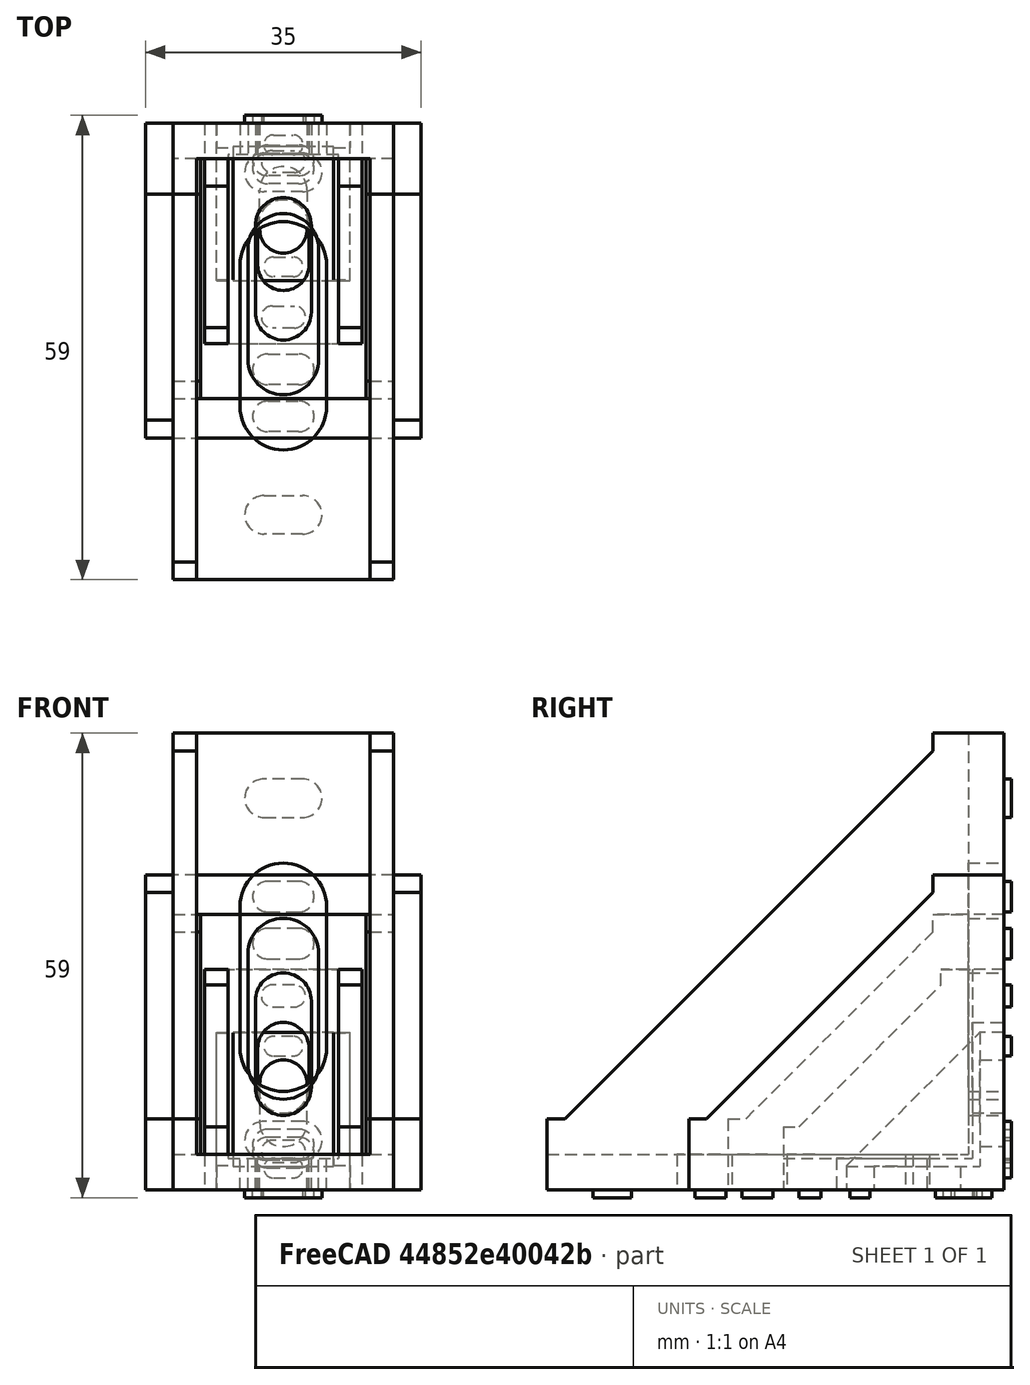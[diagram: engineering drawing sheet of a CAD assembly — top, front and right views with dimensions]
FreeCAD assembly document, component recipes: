
FREECAD ASSEMBLY — COMPONENT RECIPES ("Corner_bracket")

This assembly document has 5 components, labeled P0..P4 below (a component is one placed body or linked part). 5 of them carry a construction recipe — the FreeCAD feature program that regenerates the part from scratch, quoted from this document or its linked companion documents; the rest are supplied as boundary geometry only. No exploded tour is included for this assembly.
COMPONENT P0 — recipe-attached ("Corner bracket001", modeled in this document).
Construction recipe (the document's own serialized feature program — sketch geometry with constraints, then the solid features built on it; lengths are millimeters unless a unit is written):

FEATURE [PartDesign::Plane] DatumPlane001
  AttachmentOffset = pos=(0,0,0) rot=(1,0,0;0.785398rad)
  Length = 65.3219
  MapMode = 5
  Placement = pos=(0,0,0) rot=(1,0,0;2.35619rad)
  ResizeMode = 0
  Support = -> [XZ_Plane003]
  Width = 132.702
FEATURE [Sketcher::SketchObject] Sketch004
  FullyConstrained = true
  MapMode = 5
  Placement = pos=(0,0,0) rot=(1,0,0;1.5708rad)
  Support = -> [XZ_Plane003]
  expr: Constraints[7] = <<Spreadsheet001>>.E_dim
  expr: Constraints[8] = <<Spreadsheet001>>.F_dim
  expr: Constraints[9] = <<Spreadsheet001>>.H_dim
  sketch-geometry (4):
    g0: ArcOfCircle CenterX=0 CenterY=8.5 CenterZ=0 NormalX=0 NormalY=0 NormalZ=1 AngleXU=0 Radius=3 StartAngle=3.14159 EndAngle=6.28319
    g1: ArcOfCircle CenterX=0 CenterY=13.5 CenterZ=0 NormalX=0 NormalY=0 NormalZ=1 AngleXU=0 Radius=3 StartAngle=0 EndAngle=3.14159
    g2: LineSegment StartX=3 StartY=8.5 StartZ=0 EndX=3 EndY=13.5 EndZ=0
    g3: LineSegment StartX=-3 StartY=13.5 StartZ=0 EndX=-3 EndY=8.5 EndZ=0
  constraints (10):
    c: Tangent(g0,g2) = -1.5708
    c: Tangent(g2,g1) = -1.5708
    c: Tangent(g1,g3) = -1.5708
    c: Tangent(g3,g0) = -1.5708
    c: Equal(g0,g1)
    c: PointOnObject(g0,g-2)
    c: PointOnObject(g1,g-2)
    c: DistanceY(g0) = 8.5
    c: DistanceY(g2,g2) = 5
    c: Diameter(g1) = 6
FEATURE [Sketcher::SketchObject] Sketch005
  FullyConstrained = true
  MapMode = 5
  Placement = pos=(0,0,0) rot=(0.57735,0.57735,0.57735;2.0944rad)
  Support = -> [YZ_Plane003]
  expr: Constraints[10] = <<Spreadsheet001>>.A_dim
  expr: Constraints[15] = <<Spreadsheet001>>.D_aux2
  expr: Constraints[8] = <<Spreadsheet001>>.A_dim
  expr: Constraints[9] = <<Spreadsheet001>>.D_dim + <<Spreadsheet001>>.D_aux1
  sketch-geometry (7):
    g0: LineSegment StartX=0 StartY=0 StartZ=0 EndX=0 EndY=20 EndZ=0
    g1: LineSegment StartX=0 StartY=20 StartZ=0 EndX=-3.1 EndY=20 EndZ=0
    g2: LineSegment StartX=-20 StartY=3.1 StartZ=0 EndX=-20 EndY=0 EndZ=0
    g3: LineSegment StartX=-20 StartY=0 StartZ=0 EndX=0 EndY=0 EndZ=0
    g4: LineSegment StartX=-20 StartY=3.1 StartZ=0 EndX=-19.9 EndY=3.1 EndZ=0
    g5: LineSegment StartX=-19.9 StartY=3.1 StartZ=0 EndX=-3.1 EndY=19.9 EndZ=0
    g6: LineSegment StartX=-3.1 StartY=19.9 StartZ=0 EndX=-3.1 EndY=20 EndZ=0
  constraints (20):
    c: Coincident(g-1,g0)
    c: PointOnObject(g0,g-2)
    c: Coincident(g0,g1)
    c: Horizontal(g1)
    c: PointOnObject(g2,g-1)
    c: Vertical(g2)
    c: Coincident(g2,g3)
    c: Coincident(g3,g0)
    c: DistanceY(g0,g0) = 20
    c: DistanceX(g1,g1) = 3.1
    c: DistanceX(g3,g3) = 20
    c: Coincident(g2,g4)
    c: Horizontal(g4)
    c: Coincident(g4,g5)
    c: Equal(g2,g1)
    c: DistanceX(g4,g4) = 0.1
    c: Angle(g5) = 0.785398
    c: Coincident(g6,g5)
    c: Coincident(g6,g1)
    c: Vertical(g6)
FEATURE [PartDesign::Pad] Pad002
  Direction = (1,-2e-16,3e-16)
  Length = 17
  Length2 = 100
  Midplane = true
  Placement = pos=(0,0,0) rot=(0.57735,0.57735,0.57735;2.0944rad)
  Profile = -> Sketch005
  ReferenceAxis = -> Sketch005 [N_Axis]
  Type = 0
  expr: Length = <<Spreadsheet001>>.B_dim
FEATURE [Sketcher::SketchObject] Sketch006
  ExternalGeometry = -> [Pad002]
  FullyConstrained = true
  MapMode = 5
  Placement = pos=(-7.8e-15,1.11e-14,20) rot=(0,0,-1;1.5708rad)
  Support = -> [Pad002]
  expr: Constraints[10] = <<Spreadsheet001>>.D_dim
  expr: Constraints[12] = <<Spreadsheet001>>.C_dim
  sketch-geometry (5):
    g0: LineSegment StartX=20 StartY=-6.4 StartZ=0 EndX=20 EndY=6.4 EndZ=0
    g1: LineSegment StartX=20 StartY=6.4 StartZ=0 EndX=3 EndY=6.4 EndZ=0
    g2: LineSegment StartX=3 StartY=6.4 StartZ=0 EndX=3 EndY=-6.4 EndZ=0
    g3: LineSegment StartX=3 StartY=-6.4 StartZ=0 EndX=20 EndY=-6.4 EndZ=0
    g4: GeomPoint X=11.5 Y=0 Z=0
  constraints (13):
    c: Coincident(g0,g1)
    c: Coincident(g1,g2)
    c: Coincident(g2,g3)
    c: Coincident(g3,g0)
    c: Horizontal(g1)
    c: Horizontal(g3)
    c: Vertical(g0)
    c: Vertical(g2)
    c: Symmetric(g1,g0,g4)
    c: PointOnObject(g4,g-1)
    c: DistanceX(g1) = 3
    c: Vertical(g0,g-3)
    c: DistanceY(g0,g0) = 12.8
FEATURE [PartDesign::Pocket] Pocket002
  BaseFeature = -> Pad002
  Direction = (4e-16,-6e-16,-1)
  Length = 17
  Length2 = 5
  Placement = pos=(0,0,0) rot=(0.57735,0.57735,0.57735;2.0944rad)
  Profile = -> Sketch006
  ReferenceAxis = -> Sketch006 [N_Axis]
  Type = 0
  expr: Length = <<Spreadsheet001>>.A_dim - <<Spreadsheet001>>.D_dim
FEATURE [PartDesign::Pocket] Pocket003
  BaseFeature = -> Pocket002
  Direction = (0,1,2e-16)
  Length = 5
  Length2 = 5
  Placement = pos=(0,0,0) rot=(0.57735,0.57735,0.57735;2.0944rad)
  Profile = -> Sketch004
  ReferenceAxis = -> Sketch004 [N_Axis]
  Reversed = true
  Type = 2
FEATURE [Sketcher::SketchObject] Sketch007
  FullyConstrained = true
  MapMode = 5
  Placement = pos=(0,0,0) rot=(1,0,0;1.5708rad)
  Support = -> [XZ_Plane003]
  expr: Constraints[14] = <<Spreadsheet001>>.G_dim / 2
  expr: Constraints[15] = <<Spreadsheet001>>.G_dim / 4
  expr: Constraints[16] = (<<Spreadsheet001>>.E_dim - <<Spreadsheet001>>.H_dim / 2) / 2
  expr: Constraints[17] = (<<Spreadsheet001>>.A_dim + <<Spreadsheet001>>.E_dim + <<Spreadsheet001>>.F_dim + <<Spreadsheet001>>.H_dim / 2) / 2
  sketch-geometry (8):
    g0: ArcOfCircle CenterX=-1.25 CenterY=2.75 CenterZ=0 NormalX=0 NormalY=0 NormalZ=1 AngleXU=0 Radius=1.25 StartAngle=1.5708 EndAngle=4.71239
    g1: ArcOfCircle CenterX=1.25 CenterY=2.75 CenterZ=0 NormalX=0 NormalY=0 NormalZ=1 AngleXU=0 Radius=1.25 StartAngle=4.71239 EndAngle=7.85398
    g2: LineSegment StartX=-1.25 StartY=1.5 StartZ=0 EndX=1.25 EndY=1.5 EndZ=0
    g3: LineSegment StartX=1.25 StartY=4 StartZ=0 EndX=-1.25 EndY=4 EndZ=0
    g4: ArcOfCircle CenterX=-1.25 CenterY=18.25 CenterZ=0 NormalX=0 NormalY=0 NormalZ=1 AngleXU=0 Radius=1.25 StartAngle=1.5708 EndAngle=4.71239
    g5: ArcOfCircle CenterX=1.25 CenterY=18.25 CenterZ=0 NormalX=0 NormalY=0 NormalZ=1 AngleXU=0 Radius=1.25 StartAngle=4.71239 EndAngle=7.85398
    g6: LineSegment StartX=-1.25 StartY=17 StartZ=0 EndX=1.25 EndY=17 EndZ=0
    g7: LineSegment StartX=1.25 StartY=19.5 StartZ=0 EndX=-1.25 EndY=19.5 EndZ=0
  constraints (18):
    c: Tangent(g0,g2) = -1.5708
    c: Tangent(g2,g1) = -1.5708
    c: Tangent(g1,g3) = -1.5708
    c: Tangent(g3,g0) = -1.5708
    c: Equal(g0,g1)
    c: Tangent(g4,g6) = -1.5708
    c: Tangent(g6,g5) = -1.5708
    c: Tangent(g5,g7) = -1.5708
    c: Tangent(g7,g4) = -1.5708
    c: Equal(g4,g5)
    c: Symmetric(g1,g0,g-2)
    c: Symmetric(g4,g5,g-2)
    c: Equal(g7,g2)
    c: Equal(g1,g5)
    c: DistanceX(g7,g7) = 2.5
    c: Radius(g5) = 1.25
    c: DistanceY(g1) = 2.75
    c: DistanceY(g4) = 18.25
FEATURE [PartDesign::Pad] Pad003
  BaseFeature = -> Pocket003
  Direction = (0,-1,-2e-16)
  Length = 1
  Length2 = 10
  Placement = pos=(0,0,0) rot=(0.57735,0.57735,0.57735;2.0944rad)
  Profile = -> Sketch007
  ReferenceAxis = -> Sketch007 [N_Axis]
  Reversed = true
  Type = 0
FEATURE [PartDesign::Mirrored] Mirrored001
  BaseFeature = -> Pad003
  MirrorPlane = -> DatumPlane001
  Originals = -> [Pocket003,Pad003]
  Placement = pos=(0,0,0) rot=(0.57735,0.57735,0.57735;2.0944rad)
FEATURE [PartDesign::Body] Body001  label="Corner bracket 20x20"
  Group = -> [Sketch005,Pad002,Sketch006,Pocket002,Sketch004,Pocket003,Sketch007,Pad003,DatumPlane001,Mirrored001]
  Origin = -> Origin003
  Tip = -> Mirrored001
  expr: Label = <<Corner bracket %s>> % Spreadsheet001.A_dim + <<x%s>> % Spreadsheet001.A_dim
COMPONENT P1 — recipe-attached ("Corner bracket002", modeled in this document).
Construction recipe (the document's own serialized feature program — sketch geometry with constraints, then the solid features built on it; lengths are millimeters unless a unit is written):

FEATURE [PartDesign::Plane] DatumPlane002
  AttachmentOffset = pos=(0,0,0) rot=(1,0,0;0.785398rad)
  Length = 65.3219
  MapMode = 5
  Placement = pos=(0,0,0) rot=(1,0,0;2.35619rad)
  ResizeMode = 0
  Support = -> [XZ_Plane005]
  Width = 132.702
FEATURE [Sketcher::SketchObject] Sketch008
  FullyConstrained = true
  MapMode = 5
  Placement = pos=(0,0,0) rot=(1,0,0;1.5708rad)
  Support = -> [XZ_Plane005]
  expr: Constraints[7] = <<Spreadsheet002>>.E_dim
  expr: Constraints[8] = <<Spreadsheet002>>.F_dim
  expr: Constraints[9] = <<Spreadsheet002>>.H_dim
  sketch-geometry (4):
    g0: ArcOfCircle CenterX=0 CenterY=13 CenterZ=0 NormalX=0 NormalY=0 NormalZ=1 AngleXU=0 Radius=3.25 StartAngle=3.14159 EndAngle=6.28319
    g1: ArcOfCircle CenterX=0 CenterY=18 CenterZ=0 NormalX=0 NormalY=0 NormalZ=1 AngleXU=0 Radius=3.25 StartAngle=7.603e-13 EndAngle=3.14159
    g2: LineSegment StartX=3.25 StartY=13 StartZ=0 EndX=3.25 EndY=18 EndZ=0
    g3: LineSegment StartX=-3.25 StartY=18 StartZ=0 EndX=-3.25 EndY=13 EndZ=0
  constraints (10):
    c: Tangent(g0,g2) = -1.5708
    c: Tangent(g2,g1) = -1.5708
    c: Tangent(g1,g3) = -1.5708
    c: Tangent(g3,g0) = -1.5708
    c: Equal(g0,g1)
    c: PointOnObject(g0,g-2)
    c: PointOnObject(g1,g-2)
    c: DistanceY(g0) = 13
    c: DistanceY(g2,g2) = 5
    c: Diameter(g1) = 6.5
FEATURE [Sketcher::SketchObject] Sketch009
  FullyConstrained = true
  MapMode = 5
  Placement = pos=(0,0,0) rot=(0.57735,0.57735,0.57735;2.0944rad)
  Support = -> [YZ_Plane005]
  expr: Constraints[10] = <<Spreadsheet002>>.A_dim
  expr: Constraints[15] = <<Spreadsheet002>>.D_aux2
  expr: Constraints[8] = <<Spreadsheet002>>.A_dim
  expr: Constraints[9] = <<Spreadsheet002>>.D_dim + <<Spreadsheet002>>.D_aux1
  sketch-geometry (7):
    g0: LineSegment StartX=0 StartY=0 StartZ=0 EndX=0 EndY=28 EndZ=0
    g1: LineSegment StartX=0 StartY=28 StartZ=0 EndX=-8 EndY=28 EndZ=0
    g2: LineSegment StartX=-28 StartY=8 StartZ=0 EndX=-28 EndY=0 EndZ=0
    g3: LineSegment StartX=-28 StartY=0 StartZ=0 EndX=0 EndY=0 EndZ=0
    g4: LineSegment StartX=-28 StartY=8 StartZ=0 EndX=-26 EndY=8 EndZ=0
    g5: LineSegment StartX=-26 StartY=8 StartZ=0 EndX=-8 EndY=26 EndZ=0
    g6: LineSegment StartX=-8 StartY=26 StartZ=0 EndX=-8 EndY=28 EndZ=0
  constraints (20):
    c: Coincident(g-1,g0)
    c: PointOnObject(g0,g-2)
    c: Coincident(g0,g1)
    c: Horizontal(g1)
    c: PointOnObject(g2,g-1)
    c: Vertical(g2)
    c: Coincident(g2,g3)
    c: Coincident(g3,g0)
    c: DistanceY(g0,g0) = 28
    c: DistanceX(g1,g1) = 8
    c: DistanceX(g3,g3) = 28
    c: Coincident(g2,g4)
    c: Horizontal(g4)
    c: Coincident(g4,g5)
    c: Equal(g2,g1)
    c: DistanceX(g4,g4) = 2
    c: Angle(g5) = 0.785398
    c: Coincident(g6,g5)
    c: Coincident(g6,g1)
    c: Vertical(g6)
FEATURE [PartDesign::Pad] Pad004
  Direction = (1,-2e-16,3e-16)
  Length = 20
  Length2 = 100
  Midplane = true
  Placement = pos=(0,0,0) rot=(0.57735,0.57735,0.57735;2.0944rad)
  Profile = -> Sketch009
  ReferenceAxis = -> Sketch009 [N_Axis]
  Type = 0
  expr: Length = <<Spreadsheet002>>.B_dim
FEATURE [Sketcher::SketchObject] Sketch010
  ExternalGeometry = -> [Pad004]
  FullyConstrained = true
  MapMode = 5
  Placement = pos=(-1.09e-14,1.55e-14,28) rot=(0,0,-1;1.5708rad)
  Support = -> [Pad004]
  expr: Constraints[10] = <<Spreadsheet002>>.D_dim
  expr: Constraints[12] = <<Spreadsheet002>>.C_dim
  sketch-geometry (5):
    g0: LineSegment StartX=28 StartY=-7 StartZ=0 EndX=28 EndY=7 EndZ=0
    g1: LineSegment StartX=28 StartY=7 StartZ=0 EndX=4 EndY=7 EndZ=0
    g2: LineSegment StartX=4 StartY=7 StartZ=0 EndX=4 EndY=-7 EndZ=0
    g3: LineSegment StartX=4 StartY=-7 StartZ=0 EndX=28 EndY=-7 EndZ=0
    g4: GeomPoint X=16 Y=0 Z=0
  constraints (13):
    c: Coincident(g0,g1)
    c: Coincident(g1,g2)
    c: Coincident(g2,g3)
    c: Coincident(g3,g0)
    c: Horizontal(g1)
    c: Horizontal(g3)
    c: Vertical(g0)
    c: Vertical(g2)
    c: Symmetric(g1,g0,g4)
    c: PointOnObject(g4,g-1)
    c: DistanceX(g1) = 4
    c: Vertical(g0,g-3)
    c: DistanceY(g0,g0) = 14
FEATURE [PartDesign::Pocket] Pocket004
  BaseFeature = -> Pad004
  Direction = (4e-16,-6e-16,-1)
  Length = 24
  Length2 = 5
  Placement = pos=(0,0,0) rot=(0.57735,0.57735,0.57735;2.0944rad)
  Profile = -> Sketch010
  ReferenceAxis = -> Sketch010 [N_Axis]
  Type = 0
  expr: Length = <<Spreadsheet002>>.A_dim - <<Spreadsheet002>>.D_dim
FEATURE [PartDesign::Pocket] Pocket005
  BaseFeature = -> Pocket004
  Direction = (0,1,2e-16)
  Length = 5
  Length2 = 5
  Placement = pos=(0,0,0) rot=(0.57735,0.57735,0.57735;2.0944rad)
  Profile = -> Sketch008
  ReferenceAxis = -> Sketch008 [N_Axis]
  Reversed = true
  Type = 2
FEATURE [Sketcher::SketchObject] Sketch011
  FullyConstrained = true
  MapMode = 5
  Placement = pos=(0,0,0) rot=(1,0,0;1.5708rad)
  Support = -> [XZ_Plane005]
  expr: Constraints[14] = <<Spreadsheet002>>.G_dim / 2
  expr: Constraints[15] = <<Spreadsheet002>>.G_dim / 4
  expr: Constraints[16] = (<<Spreadsheet002>>.E_dim - <<Spreadsheet002>>.H_dim / 2) / 2
  expr: Constraints[17] = (<<Spreadsheet002>>.A_dim + <<Spreadsheet002>>.E_dim + <<Spreadsheet002>>.F_dim + <<Spreadsheet002>>.H_dim / 2) / 2
  sketch-geometry (8):
    g0: ArcOfCircle CenterX=-1.4 CenterY=4.875 CenterZ=0 NormalX=0 NormalY=0 NormalZ=1 AngleXU=0 Radius=1.4 StartAngle=1.5708 EndAngle=4.71239
    g1: ArcOfCircle CenterX=1.4 CenterY=4.875 CenterZ=0 NormalX=0 NormalY=0 NormalZ=1 AngleXU=0 Radius=1.4 StartAngle=4.71239 EndAngle=7.85398
    g2: LineSegment StartX=-1.4 StartY=3.475 StartZ=0 EndX=1.4 EndY=3.475 EndZ=0
    g3: LineSegment StartX=1.4 StartY=6.275 StartZ=0 EndX=-1.4 EndY=6.275 EndZ=0
    g4: ArcOfCircle CenterX=-1.4 CenterY=24.625 CenterZ=0 NormalX=0 NormalY=0 NormalZ=1 AngleXU=0 Radius=1.4 StartAngle=1.5708 EndAngle=4.71239
    g5: ArcOfCircle CenterX=1.4 CenterY=24.625 CenterZ=0 NormalX=0 NormalY=0 NormalZ=1 AngleXU=0 Radius=1.4 StartAngle=4.71239 EndAngle=7.85398
    g6: LineSegment StartX=-1.4 StartY=23.225 StartZ=0 EndX=1.4 EndY=23.225 EndZ=0
    g7: LineSegment StartX=1.4 StartY=26.025 StartZ=0 EndX=-1.4 EndY=26.025 EndZ=0
  constraints (18):
    c: Tangent(g0,g2) = -1.5708
    c: Tangent(g2,g1) = -1.5708
    c: Tangent(g1,g3) = -1.5708
    c: Tangent(g3,g0) = -1.5708
    c: Equal(g0,g1)
    c: Tangent(g4,g6) = -1.5708
    c: Tangent(g6,g5) = -1.5708
    c: Tangent(g5,g7) = -1.5708
    c: Tangent(g7,g4) = -1.5708
    c: Equal(g4,g5)
    c: Symmetric(g1,g0,g-2)
    c: Symmetric(g4,g5,g-2)
    c: Equal(g7,g2)
    c: Equal(g1,g5)
    c: DistanceX(g7,g7) = 2.8
    c: Radius(g5) = 1.4
    c: DistanceY(g1) = 4.875
    c: DistanceY(g4) = 24.625
FEATURE [PartDesign::Pad] Pad005
  BaseFeature = -> Pocket005
  Direction = (0,-1,-2e-16)
  Length = 1
  Length2 = 10
  Placement = pos=(0,0,0) rot=(0.57735,0.57735,0.57735;2.0944rad)
  Profile = -> Sketch011
  ReferenceAxis = -> Sketch011 [N_Axis]
  Reversed = true
  Type = 0
FEATURE [PartDesign::Mirrored] Mirrored002
  BaseFeature = -> Pad005
  MirrorPlane = -> DatumPlane002
  Originals = -> [Pocket005,Pad005]
  Placement = pos=(0,0,0) rot=(0.57735,0.57735,0.57735;2.0944rad)
FEATURE [PartDesign::Body] Body002  label="Corner bracket 28x28"
  Group = -> [Sketch009,Pad004,Sketch010,Pocket004,Sketch008,Pocket005,Sketch011,Pad005,DatumPlane002,Mirrored002]
  Origin = -> Origin005
  Tip = -> Mirrored002
  expr: Label = <<Corner bracket %s>> % Spreadsheet002.A_dim + <<x%s>> % Spreadsheet002.A_dim
COMPONENT P2 — recipe-attached ("Corner bracket003", modeled in this document).
Construction recipe (the document's own serialized feature program — sketch geometry with constraints, then the solid features built on it; lengths are millimeters unless a unit is written):

FEATURE [PartDesign::Plane] DatumPlane003
  AttachmentOffset = pos=(0,0,0) rot=(1,0,0;0.785398rad)
  Length = 63.0271
  MapMode = 5
  Placement = pos=(0,0,0) rot=(1,0,0;2.35619rad)
  ResizeMode = 0
  Support = -> [XZ_Plane007]
  Width = 97.8799
FEATURE [Sketcher::SketchObject] Sketch012
  FullyConstrained = true
  MapMode = 5
  Placement = pos=(0,0,0) rot=(1,0,0;1.5708rad)
  Support = -> [XZ_Plane007]
  expr: Constraints[7] = <<Spreadsheet003>>.E_dim
  expr: Constraints[8] = <<Spreadsheet003>>.F_dim
  expr: Constraints[9] = <<Spreadsheet003>>.H_dim
  sketch-geometry (4):
    g0: ArcOfCircle CenterX=0 CenterY=18 CenterZ=0 NormalX=0 NormalY=0 NormalZ=1 AngleXU=0 Radius=5.5 StartAngle=3.14159 EndAngle=6.28319
    g1: ArcOfCircle CenterX=0 CenterY=36 CenterZ=0 NormalX=0 NormalY=0 NormalZ=1 AngleXU=0 Radius=5.5 StartAngle=-5.3e-15 EndAngle=3.14159
    g2: LineSegment StartX=5.5 StartY=18 StartZ=0 EndX=5.5 EndY=36 EndZ=0
    g3: LineSegment StartX=-5.5 StartY=36 StartZ=0 EndX=-5.5 EndY=18 EndZ=0
  constraints (10):
    c: Tangent(g0,g2) = -1.5708
    c: Tangent(g2,g1) = -1.5708
    c: Tangent(g1,g3) = -1.5708
    c: Tangent(g3,g0) = -1.5708
    c: Equal(g0,g1)
    c: PointOnObject(g0,g-2)
    c: PointOnObject(g1,g-2)
    c: DistanceY(g0) = 18
    c: DistanceY(g2,g2) = 18
    c: Diameter(g1) = 11
FEATURE [Sketcher::SketchObject] Sketch013
  FullyConstrained = true
  MapMode = 5
  Placement = pos=(0,0,0) rot=(0.57735,0.57735,0.57735;2.0944rad)
  Support = -> [YZ_Plane007]
  expr: Constraints[10] = <<Spreadsheet003>>.A_dim
  expr: Constraints[15] = <<Spreadsheet003>>.D_aux2
  expr: Constraints[8] = <<Spreadsheet003>>.A_dim
  expr: Constraints[9] = <<Spreadsheet003>>.D_dim + <<Spreadsheet003>>.D_aux1
  sketch-geometry (7):
    g0: LineSegment StartX=0 StartY=0 StartZ=0 EndX=0 EndY=58 EndZ=0
    g1: LineSegment StartX=0 StartY=58 StartZ=0 EndX=-9 EndY=58 EndZ=0
    g2: LineSegment StartX=-58 StartY=9 StartZ=0 EndX=-58 EndY=0 EndZ=0
    g3: LineSegment StartX=-58 StartY=0 StartZ=0 EndX=0 EndY=0 EndZ=0
    g4: LineSegment StartX=-58 StartY=9 StartZ=0 EndX=-55.75 EndY=9 EndZ=0
    g5: LineSegment StartX=-55.75 StartY=9 StartZ=0 EndX=-9 EndY=55.75 EndZ=0
    g6: LineSegment StartX=-9 StartY=55.75 StartZ=0 EndX=-9 EndY=58 EndZ=0
  constraints (20):
    c: Coincident(g-1,g0)
    c: PointOnObject(g0,g-2)
    c: Coincident(g0,g1)
    c: Horizontal(g1)
    c: PointOnObject(g2,g-1)
    c: Vertical(g2)
    c: Coincident(g2,g3)
    c: Coincident(g3,g0)
    c: DistanceY(g0,g0) = 58
    c: DistanceX(g1,g1) = 9
    c: DistanceX(g3,g3) = 58
    c: Coincident(g2,g4)
    c: Horizontal(g4)
    c: Coincident(g4,g5)
    c: Equal(g2,g1)
    c: DistanceX(g4,g4) = 2.25
    c: Angle(g5) = 0.785398
    c: Coincident(g6,g5)
    c: Coincident(g6,g1)
    c: Vertical(g6)
FEATURE [PartDesign::Pad] Pad006
  Direction = (1,-2e-16,3e-16)
  Length = 28
  Length2 = 100
  Midplane = true
  Placement = pos=(0,0,0) rot=(0.57735,0.57735,0.57735;2.0944rad)
  Profile = -> Sketch013
  ReferenceAxis = -> Sketch013 [N_Axis]
  Type = 0
  expr: Length = <<Spreadsheet003>>.B_dim
FEATURE [Sketcher::SketchObject] Sketch014
  ExternalGeometry = -> [Pad006]
  FullyConstrained = true
  MapMode = 5
  Placement = pos=(-2.25e-14,3.22e-14,58) rot=(0,0,-1;1.5708rad)
  Support = -> [Pad006]
  expr: Constraints[10] = <<Spreadsheet003>>.D_dim
  expr: Constraints[12] = <<Spreadsheet003>>.C_dim
  sketch-geometry (5):
    g0: LineSegment StartX=58 StartY=-11 StartZ=0 EndX=58 EndY=11 EndZ=0
    g1: LineSegment StartX=58 StartY=11 StartZ=0 EndX=4.5 EndY=11 EndZ=0
    g2: LineSegment StartX=4.5 StartY=11 StartZ=0 EndX=4.5 EndY=-11 EndZ=0
    g3: LineSegment StartX=4.5 StartY=-11 StartZ=0 EndX=58 EndY=-11 EndZ=0
    g4: GeomPoint X=31.25 Y=0 Z=0
  constraints (13):
    c: Coincident(g0,g1)
    c: Coincident(g1,g2)
    c: Coincident(g2,g3)
    c: Coincident(g3,g0)
    c: Horizontal(g1)
    c: Horizontal(g3)
    c: Vertical(g0)
    c: Vertical(g2)
    c: Symmetric(g1,g0,g4)
    c: PointOnObject(g4,g-1)
    c: DistanceX(g1) = 4.5
    c: Vertical(g0,g-3)
    c: DistanceY(g0,g0) = 22
FEATURE [PartDesign::Pocket] Pocket006
  BaseFeature = -> Pad006
  Direction = (4e-16,-6e-16,-1)
  Length = 53.5
  Length2 = 5
  Placement = pos=(0,0,0) rot=(0.57735,0.57735,0.57735;2.0944rad)
  Profile = -> Sketch014
  ReferenceAxis = -> Sketch014 [N_Axis]
  Type = 0
  expr: Length = <<Spreadsheet003>>.A_dim - <<Spreadsheet003>>.D_dim
FEATURE [PartDesign::Pocket] Pocket007
  BaseFeature = -> Pocket006
  Direction = (0,1,2e-16)
  Length = 5
  Length2 = 5
  Placement = pos=(0,0,0) rot=(0.57735,0.57735,0.57735;2.0944rad)
  Profile = -> Sketch012
  ReferenceAxis = -> Sketch012 [N_Axis]
  Reversed = true
  Type = 2
FEATURE [Sketcher::SketchObject] Sketch015
  FullyConstrained = true
  MapMode = 5
  Placement = pos=(0,0,0) rot=(1,0,0;1.5708rad)
  Support = -> [XZ_Plane007]
  expr: Constraints[14] = <<Spreadsheet003>>.G_dim / 2
  expr: Constraints[15] = <<Spreadsheet003>>.G_dim / 4
  expr: Constraints[16] = (<<Spreadsheet003>>.E_dim - <<Spreadsheet003>>.H_dim / 2) / 2
  expr: Constraints[17] = (<<Spreadsheet003>>.A_dim + <<Spreadsheet003>>.E_dim + <<Spreadsheet003>>.F_dim + <<Spreadsheet003>>.H_dim / 2) / 2
  sketch-geometry (8):
    g0: ArcOfCircle CenterX=-2.45 CenterY=6.25 CenterZ=0 NormalX=0 NormalY=0 NormalZ=1 AngleXU=0 Radius=2.45 StartAngle=1.5708 EndAngle=4.71239
    g1: ArcOfCircle CenterX=2.45 CenterY=6.25 CenterZ=0 NormalX=0 NormalY=0 NormalZ=1 AngleXU=0 Radius=2.45 StartAngle=4.71239 EndAngle=7.85398
    g2: LineSegment StartX=-2.45 StartY=3.8 StartZ=0 EndX=2.45 EndY=3.8 EndZ=0
    g3: LineSegment StartX=2.45 StartY=8.7 StartZ=0 EndX=-2.45 EndY=8.7 EndZ=0
    g4: ArcOfCircle CenterX=-2.45 CenterY=49.75 CenterZ=0 NormalX=0 NormalY=0 NormalZ=1 AngleXU=0 Radius=2.45 StartAngle=1.5708 EndAngle=4.71239
    g5: ArcOfCircle CenterX=2.45 CenterY=49.75 CenterZ=0 NormalX=0 NormalY=0 NormalZ=1 AngleXU=0 Radius=2.45 StartAngle=4.71239 EndAngle=7.85398
    g6: LineSegment StartX=-2.45 StartY=47.3 StartZ=0 EndX=2.45 EndY=47.3 EndZ=0
    g7: LineSegment StartX=2.45 StartY=52.2 StartZ=0 EndX=-2.45 EndY=52.2 EndZ=0
  constraints (18):
    c: Tangent(g0,g2) = -1.5708
    c: Tangent(g2,g1) = -1.5708
    c: Tangent(g1,g3) = -1.5708
    c: Tangent(g3,g0) = -1.5708
    c: Equal(g0,g1)
    c: Tangent(g4,g6) = -1.5708
    c: Tangent(g6,g5) = -1.5708
    c: Tangent(g5,g7) = -1.5708
    c: Tangent(g7,g4) = -1.5708
    c: Equal(g4,g5)
    c: Symmetric(g1,g0,g-2)
    c: Symmetric(g4,g5,g-2)
    c: Equal(g7,g2)
    c: Equal(g1,g5)
    c: DistanceX(g7,g7) = 4.9
    c: Radius(g5) = 2.45
    c: DistanceY(g1) = 6.25
    c: DistanceY(g4) = 49.75
FEATURE [PartDesign::Pad] Pad007
  BaseFeature = -> Pocket007
  Direction = (0,-1,-2e-16)
  Length = 1
  Length2 = 10
  Placement = pos=(0,0,0) rot=(0.57735,0.57735,0.57735;2.0944rad)
  Profile = -> Sketch015
  ReferenceAxis = -> Sketch015 [N_Axis]
  Reversed = true
  Type = 0
FEATURE [PartDesign::Mirrored] Mirrored003
  BaseFeature = -> Pad007
  MirrorPlane = -> DatumPlane003
  Originals = -> [Pocket007,Pad007]
  Placement = pos=(0,0,0) rot=(0.57735,0.57735,0.57735;2.0944rad)
FEATURE [PartDesign::Body] Body003  label="Corner bracket 58x58"
  Group = -> [Sketch013,Pad006,Sketch014,Pocket006,Sketch012,Pocket007,Sketch015,Pad007,DatumPlane003,Mirrored003]
  Origin = -> Origin007
  Tip = -> Mirrored003
  expr: Label = <<Corner bracket %s>> % Spreadsheet003.A_dim + <<x%s>> % Spreadsheet003.A_dim
COMPONENT P3 — recipe-attached ("Corner bracket004", modeled in this document).
Construction recipe (the document's own serialized feature program — sketch geometry with constraints, then the solid features built on it; lengths are millimeters unless a unit is written):

FEATURE [PartDesign::Plane] DatumPlane004
  AttachmentOffset = pos=(0,0,0) rot=(1,0,0;0.785398rad)
  Length = 63.0271
  MapMode = 5
  Placement = pos=(0,0,0) rot=(1,0,0;2.35619rad)
  ResizeMode = 0
  Support = -> [XZ_Plane009]
  Width = 97.8799
FEATURE [Sketcher::SketchObject] Sketch016
  FullyConstrained = true
  MapMode = 5
  Placement = pos=(0,0,0) rot=(1,0,0;1.5708rad)
  Support = -> [XZ_Plane009]
  expr: Constraints[7] = <<Spreadsheet004>>.E_dim
  expr: Constraints[8] = <<Spreadsheet004>>.F_dim
  expr: Constraints[9] = <<Spreadsheet004>>.H_dim
  sketch-geometry (4):
    g0: ArcOfCircle CenterX=0 CenterY=16 CenterZ=0 NormalX=0 NormalY=0 NormalZ=1 AngleXU=0 Radius=4.5 StartAngle=3.14159 EndAngle=6.28319
    g1: ArcOfCircle CenterX=0 CenterY=30 CenterZ=0 NormalX=0 NormalY=0 NormalZ=1 AngleXU=0 Radius=4.5 StartAngle=4.0227e-12 EndAngle=3.14159
    g2: LineSegment StartX=4.5 StartY=16 StartZ=0 EndX=4.5 EndY=30 EndZ=0
    g3: LineSegment StartX=-4.5 StartY=30 StartZ=0 EndX=-4.5 EndY=16 EndZ=0
  constraints (10):
    c: Tangent(g0,g2) = -1.5708
    c: Tangent(g2,g1) = -1.5708
    c: Tangent(g1,g3) = -1.5708
    c: Tangent(g3,g0) = -1.5708
    c: Equal(g0,g1)
    c: PointOnObject(g0,g-2)
    c: PointOnObject(g1,g-2)
    c: DistanceY(g0) = 16
    c: DistanceY(g2,g2) = 14
    c: Diameter(g1) = 9
FEATURE [Sketcher::SketchObject] Sketch017
  FullyConstrained = true
  MapMode = 5
  Placement = pos=(0,0,0) rot=(0.57735,0.57735,0.57735;2.0944rad)
  Support = -> [YZ_Plane009]
  expr: Constraints[10] = <<Spreadsheet004>>.A_dim
  expr: Constraints[15] = <<Spreadsheet004>>.D_aux2
  expr: Constraints[8] = <<Spreadsheet004>>.A_dim
  expr: Constraints[9] = <<Spreadsheet004>>.D_dim + <<Spreadsheet004>>.D_aux1
  sketch-geometry (7):
    g0: LineSegment StartX=0 StartY=0 StartZ=0 EndX=0 EndY=40 EndZ=0
    g1: LineSegment StartX=0 StartY=40 StartZ=0 EndX=-9 EndY=40 EndZ=0
    g2: LineSegment StartX=-40 StartY=9 StartZ=0 EndX=-40 EndY=0 EndZ=0
    g3: LineSegment StartX=-40 StartY=0 StartZ=0 EndX=0 EndY=0 EndZ=0
    g4: LineSegment StartX=-40 StartY=9 StartZ=0 EndX=-37.75 EndY=9 EndZ=0
    g5: LineSegment StartX=-37.75 StartY=9 StartZ=0 EndX=-9 EndY=37.75 EndZ=0
    g6: LineSegment StartX=-9 StartY=37.75 StartZ=0 EndX=-9 EndY=40 EndZ=0
  constraints (20):
    c: Coincident(g-1,g0)
    c: PointOnObject(g0,g-2)
    c: Coincident(g0,g1)
    c: Horizontal(g1)
    c: PointOnObject(g2,g-1)
    c: Vertical(g2)
    c: Coincident(g2,g3)
    c: Coincident(g3,g0)
    c: DistanceY(g0,g0) = 40
    c: DistanceX(g1,g1) = 9
    c: DistanceX(g3,g3) = 40
    c: Coincident(g2,g4)
    c: Horizontal(g4)
    c: Coincident(g4,g5)
    c: Equal(g2,g1)
    c: DistanceX(g4,g4) = 2.25
    c: Angle(g5) = 0.785398
    c: Coincident(g6,g5)
    c: Coincident(g6,g1)
    c: Vertical(g6)
FEATURE [PartDesign::Pad] Pad008
  Direction = (1,-2e-16,3e-16)
  Length = 35
  Length2 = 100
  Midplane = true
  Placement = pos=(0,0,0) rot=(0.57735,0.57735,0.57735;2.0944rad)
  Profile = -> Sketch017
  ReferenceAxis = -> Sketch017 [N_Axis]
  Type = 0
  expr: Length = <<Spreadsheet004>>.B_dim
FEATURE [Sketcher::SketchObject] Sketch018
  ExternalGeometry = -> [Pad008]
  FullyConstrained = true
  MapMode = 5
  Placement = pos=(-1.55e-14,2.22e-14,40) rot=(0,0,-1;1.5708rad)
  Support = -> [Pad008]
  expr: Constraints[10] = <<Spreadsheet004>>.D_dim
  expr: Constraints[12] = <<Spreadsheet004>>.C_dim
  sketch-geometry (5):
    g0: LineSegment StartX=40 StartY=-14 StartZ=0 EndX=40 EndY=14 EndZ=0
    g1: LineSegment StartX=40 StartY=14 StartZ=0 EndX=4.5 EndY=14 EndZ=0
    g2: LineSegment StartX=4.5 StartY=14 StartZ=0 EndX=4.5 EndY=-14 EndZ=0
    g3: LineSegment StartX=4.5 StartY=-14 StartZ=0 EndX=40 EndY=-14 EndZ=0
    g4: GeomPoint X=22.25 Y=0 Z=0
  constraints (13):
    c: Coincident(g0,g1)
    c: Coincident(g1,g2)
    c: Coincident(g2,g3)
    c: Coincident(g3,g0)
    c: Horizontal(g1)
    c: Horizontal(g3)
    c: Vertical(g0)
    c: Vertical(g2)
    c: Symmetric(g1,g0,g4)
    c: PointOnObject(g4,g-1)
    c: DistanceX(g1) = 4.5
    c: Vertical(g0,g-3)
    c: DistanceY(g0,g0) = 28
FEATURE [PartDesign::Pocket] Pocket008
  BaseFeature = -> Pad008
  Direction = (4e-16,-6e-16,-1)
  Length = 35.5
  Length2 = 5
  Placement = pos=(0,0,0) rot=(0.57735,0.57735,0.57735;2.0944rad)
  Profile = -> Sketch018
  ReferenceAxis = -> Sketch018 [N_Axis]
  Type = 0
  expr: Length = <<Spreadsheet004>>.A_dim - <<Spreadsheet004>>.D_dim
FEATURE [PartDesign::Pocket] Pocket009
  BaseFeature = -> Pocket008
  Direction = (0,1,2e-16)
  Length = 5
  Length2 = 5
  Placement = pos=(0,0,0) rot=(0.57735,0.57735,0.57735;2.0944rad)
  Profile = -> Sketch016
  ReferenceAxis = -> Sketch016 [N_Axis]
  Reversed = true
  Type = 2
FEATURE [Sketcher::SketchObject] Sketch019
  FullyConstrained = true
  MapMode = 5
  Placement = pos=(0,0,0) rot=(1,0,0;1.5708rad)
  Support = -> [XZ_Plane009]
  expr: Constraints[14] = <<Spreadsheet004>>.G_dim / 2
  expr: Constraints[15] = <<Spreadsheet004>>.G_dim / 4
  expr: Constraints[16] = (<<Spreadsheet004>>.E_dim - <<Spreadsheet004>>.H_dim / 2) / 2
  expr: Constraints[17] = (<<Spreadsheet004>>.A_dim + <<Spreadsheet004>>.E_dim + <<Spreadsheet004>>.F_dim + <<Spreadsheet004>>.H_dim / 2) / 2
  sketch-geometry (8):
    g0: ArcOfCircle CenterX=-1.95 CenterY=5.75 CenterZ=0 NormalX=0 NormalY=0 NormalZ=1 AngleXU=0 Radius=1.95 StartAngle=1.5708 EndAngle=4.71239
    g1: ArcOfCircle CenterX=1.95 CenterY=5.75 CenterZ=0 NormalX=0 NormalY=0 NormalZ=1 AngleXU=0 Radius=1.95 StartAngle=4.71239 EndAngle=7.85398
    g2: LineSegment StartX=-1.95 StartY=3.8 StartZ=0 EndX=1.95 EndY=3.8 EndZ=0
    g3: LineSegment StartX=1.95 StartY=7.7 StartZ=0 EndX=-1.95 EndY=7.7 EndZ=0
    g4: ArcOfCircle CenterX=-1.95 CenterY=37.25 CenterZ=0 NormalX=0 NormalY=0 NormalZ=1 AngleXU=0 Radius=1.95 StartAngle=1.5708 EndAngle=4.71239
    g5: ArcOfCircle CenterX=1.95 CenterY=37.25 CenterZ=0 NormalX=0 NormalY=0 NormalZ=1 AngleXU=0 Radius=1.95 StartAngle=4.71239 EndAngle=7.85398
    g6: LineSegment StartX=-1.95 StartY=35.3 StartZ=0 EndX=1.95 EndY=35.3 EndZ=0
    g7: LineSegment StartX=1.95 StartY=39.2 StartZ=0 EndX=-1.95 EndY=39.2 EndZ=0
  constraints (18):
    c: Tangent(g0,g2) = -1.5708
    c: Tangent(g2,g1) = -1.5708
    c: Tangent(g1,g3) = -1.5708
    c: Tangent(g3,g0) = -1.5708
    c: Equal(g0,g1)
    c: Tangent(g4,g6) = -1.5708
    c: Tangent(g6,g5) = -1.5708
    c: Tangent(g5,g7) = -1.5708
    c: Tangent(g7,g4) = -1.5708
    c: Equal(g4,g5)
    c: Symmetric(g1,g0,g-2)
    c: Symmetric(g4,g5,g-2)
    c: Equal(g7,g2)
    c: Equal(g1,g5)
    c: DistanceX(g7,g7) = 3.9
    c: Radius(g5) = 1.95
    c: DistanceY(g1) = 5.75
    c: DistanceY(g4) = 37.25
FEATURE [PartDesign::Pad] Pad009
  BaseFeature = -> Pocket009
  Direction = (0,-1,-2e-16)
  Length = 1
  Length2 = 10
  Placement = pos=(0,0,0) rot=(0.57735,0.57735,0.57735;2.0944rad)
  Profile = -> Sketch019
  ReferenceAxis = -> Sketch019 [N_Axis]
  Reversed = true
  Type = 0
FEATURE [PartDesign::Mirrored] Mirrored004
  BaseFeature = -> Pad009
  MirrorPlane = -> DatumPlane004
  Originals = -> [Pocket009,Pad009]
  Placement = pos=(0,0,0) rot=(0.57735,0.57735,0.57735;2.0944rad)
FEATURE [PartDesign::Body] Body004  label="Corner bracket 40x041"
  Group = -> [Sketch017,Pad008,Sketch018,Pocket008,Sketch016,Pocket009,Sketch019,Pad009,DatumPlane004,Mirrored004]
  Origin = -> Origin009
  Tip = -> Mirrored004
  expr: Label = <<Corner bracket %s>> % Spreadsheet004.A_dim + <<x%s>> % Spreadsheet004.A_dim
COMPONENT P4 — recipe-attached ("Corner bracket", modeled in this document).
Construction recipe (the document's own serialized feature program — sketch geometry with constraints, then the solid features built on it; lengths are millimeters unless a unit is written):

FEATURE [Sketcher::SketchObject] Sketch
  FullyConstrained = true
  MapMode = 5
  Placement = pos=(0,0,0) rot=(0.57735,0.57735,0.57735;2.0944rad)
  Support = -> [YZ_Plane]
  expr: Constraints[10] = <<Spreadsheet>>.A_dim
  expr: Constraints[15] = <<Spreadsheet>>.D_aux2
  expr: Constraints[8] = <<Spreadsheet>>.A_dim
  expr: Constraints[9] = <<Spreadsheet>>.D_dim + <<Spreadsheet>>.D_aux1
  sketch-geometry (7):
    g0: LineSegment StartX=0 StartY=0 StartZ=0 EndX=0 EndY=35 EndZ=0
    g1: LineSegment StartX=0 StartY=35 StartZ=0 EndX=-9 EndY=35 EndZ=0
    g2: LineSegment StartX=-35 StartY=9 StartZ=0 EndX=-35 EndY=0 EndZ=0
    g3: LineSegment StartX=-35 StartY=0 StartZ=0 EndX=0 EndY=0 EndZ=0
    g4: LineSegment StartX=-35 StartY=9 StartZ=0 EndX=-32.75 EndY=9 EndZ=0
    g5: LineSegment StartX=-32.75 StartY=9 StartZ=0 EndX=-9 EndY=32.75 EndZ=0
    g6: LineSegment StartX=-9 StartY=32.75 StartZ=0 EndX=-9 EndY=35 EndZ=0
  constraints (20):
    c: Coincident(g-1,g0)
    c: PointOnObject(g0,g-2)
    c: Coincident(g0,g1)
    c: Horizontal(g1)
    c: PointOnObject(g2,g-1)
    c: Vertical(g2)
    c: Coincident(g2,g3)
    c: Coincident(g3,g0)
    c: DistanceY(g0,g0) = 35
    c: DistanceX(g1,g1) = 9
    c: DistanceX(g3,g3) = 35
    c: Coincident(g2,g4)
    c: Horizontal(g4)
    c: Coincident(g4,g5)
    c: Equal(g2,g1)
    c: DistanceX(g4,g4) = 2.25
    c: Angle(g5) = 0.785398
    c: Coincident(g6,g5)
    c: Coincident(g6,g1)
    c: Vertical(g6)
FEATURE [PartDesign::Pad] Pad
  Direction = (1,-2e-16,3e-16)
  Length = 28
  Length2 = 100
  Midplane = true
  Placement = pos=(0,0,0) rot=(0.57735,0.57735,0.57735;2.0944rad)
  Profile = -> Sketch
  ReferenceAxis = -> Sketch [N_Axis]
  Type = 0
  expr: Length = <<Spreadsheet>>.B_dim
FEATURE [Sketcher::SketchObject] Sketch001
  ExternalGeometry = -> [Pad]
  FullyConstrained = true
  MapMode = 5
  Placement = pos=(-1.36e-14,1.94e-14,35) rot=(0,0,-1;1.5708rad)
  Support = -> [Pad]
  expr: Constraints[10] = <<Spreadsheet>>.D_dim
  expr: Constraints[12] = <<Spreadsheet>>.C_dim
  sketch-geometry (5):
    g0: LineSegment StartX=35 StartY=-10.5 StartZ=0 EndX=35 EndY=10.5 EndZ=0
    g1: LineSegment StartX=35 StartY=10.5 StartZ=0 EndX=4.5 EndY=10.5 EndZ=0
    g2: LineSegment StartX=4.5 StartY=10.5 StartZ=0 EndX=4.5 EndY=-10.5 EndZ=0
    g3: LineSegment StartX=4.5 StartY=-10.5 StartZ=0 EndX=35 EndY=-10.5 EndZ=0
    g4: GeomPoint X=19.75 Y=0 Z=0
  constraints (13):
    c: Coincident(g0,g1)
    c: Coincident(g1,g2)
    c: Coincident(g2,g3)
    c: Coincident(g3,g0)
    c: Horizontal(g1)
    c: Horizontal(g3)
    c: Vertical(g0)
    c: Vertical(g2)
    c: Symmetric(g1,g0,g4)
    c: PointOnObject(g4,g-1)
    c: DistanceX(g1) = 4.5
    c: Vertical(g0,g-3)
    c: DistanceY(g0,g0) = 21
FEATURE [PartDesign::Pocket] Pocket
  BaseFeature = -> Pad
  Direction = (4e-16,-6e-16,-1)
  Length = 30.5
  Length2 = 5
  Placement = pos=(0,0,0) rot=(0.57735,0.57735,0.57735;2.0944rad)
  Profile = -> Sketch001
  ReferenceAxis = -> Sketch001 [N_Axis]
  Type = 0
  expr: Length = <<Spreadsheet>>.A_dim - <<Spreadsheet>>.D_dim
FEATURE [Sketcher::SketchObject] Sketch002
  FullyConstrained = true
  MapMode = 5
  Placement = pos=(0,0,0) rot=(1,0,0;1.5708rad)
  Support = -> [XZ_Plane]
  expr: Constraints[7] = <<Spreadsheet>>.E_dim
  expr: Constraints[8] = <<Spreadsheet>>.F_dim
  expr: Constraints[9] = <<Spreadsheet>>.H_dim
  sketch-geometry (4):
    g0: ArcOfCircle CenterX=0 CenterY=13 CenterZ=0 NormalX=0 NormalY=0 NormalZ=1 AngleXU=0 Radius=3.55 StartAngle=3.14159 EndAngle=6.28319
    g1: ArcOfCircle CenterX=0 CenterY=24 CenterZ=0 NormalX=0 NormalY=0 NormalZ=1 AngleXU=0 Radius=3.55 StartAngle=9.6e-15 EndAngle=3.14159
    g2: LineSegment StartX=3.55 StartY=13 StartZ=0 EndX=3.55 EndY=24 EndZ=0
    g3: LineSegment StartX=-3.55 StartY=24 StartZ=0 EndX=-3.55 EndY=13 EndZ=0
  constraints (10):
    c: Tangent(g0,g2) = -1.5708
    c: Tangent(g2,g1) = -1.5708
    c: Tangent(g1,g3) = -1.5708
    c: Tangent(g3,g0) = -1.5708
    c: Equal(g0,g1)
    c: PointOnObject(g0,g-2)
    c: PointOnObject(g1,g-2)
    c: DistanceY(g0) = 13
    c: DistanceY(g2,g2) = 11
    c: Diameter(g1) = 7.1
FEATURE [PartDesign::Pocket] Pocket001
  BaseFeature = -> Pocket
  Direction = (0,1,2e-16)
  Length = 5
  Length2 = 5
  Placement = pos=(0,0,0) rot=(0.57735,0.57735,0.57735;2.0944rad)
  Profile = -> Sketch002
  ReferenceAxis = -> Sketch002 [N_Axis]
  Reversed = true
  Type = 2
FEATURE [Sketcher::SketchObject] Sketch003
  FullyConstrained = true
  MapMode = 5
  Placement = pos=(0,0,0) rot=(1,0,0;1.5708rad)
  Support = -> [XZ_Plane]
  expr: Constraints[14] = <<Spreadsheet>>.G_dim / 2
  expr: Constraints[15] = <<Spreadsheet>>.G_dim / 4
  expr: Constraints[16] = (<<Spreadsheet>>.E_dim - <<Spreadsheet>>.H_dim / 2) / 2
  expr: Constraints[17] = (<<Spreadsheet>>.A_dim + <<Spreadsheet>>.E_dim + <<Spreadsheet>>.F_dim + <<Spreadsheet>>.H_dim / 2) / 2
  sketch-geometry (8):
    g0: ArcOfCircle CenterX=-1.95 CenterY=4.725 CenterZ=0 NormalX=0 NormalY=0 NormalZ=1 AngleXU=0 Radius=1.95 StartAngle=1.5708 EndAngle=4.71239
    g1: ArcOfCircle CenterX=1.95 CenterY=4.725 CenterZ=0 NormalX=0 NormalY=0 NormalZ=1 AngleXU=0 Radius=1.95 StartAngle=4.71239 EndAngle=7.85398
    g2: LineSegment StartX=-1.95 StartY=2.775 StartZ=0 EndX=1.95 EndY=2.775 EndZ=0
    g3: LineSegment StartX=1.95 StartY=6.675 StartZ=0 EndX=-1.95 EndY=6.675 EndZ=0
    g4: ArcOfCircle CenterX=-1.95 CenterY=31.275 CenterZ=0 NormalX=0 NormalY=0 NormalZ=1 AngleXU=0 Radius=1.95 StartAngle=1.5708 EndAngle=4.71239
    g5: ArcOfCircle CenterX=1.95 CenterY=31.275 CenterZ=0 NormalX=0 NormalY=0 NormalZ=1 AngleXU=0 Radius=1.95 StartAngle=4.71239 EndAngle=7.85398
    g6: LineSegment StartX=-1.95 StartY=29.325 StartZ=0 EndX=1.95 EndY=29.325 EndZ=0
    g7: LineSegment StartX=1.95 StartY=33.225 StartZ=0 EndX=-1.95 EndY=33.225 EndZ=0
  constraints (18):
    c: Tangent(g0,g2) = -1.5708
    c: Tangent(g2,g1) = -1.5708
    c: Tangent(g1,g3) = -1.5708
    c: Tangent(g3,g0) = -1.5708
    c: Equal(g0,g1)
    c: Tangent(g4,g6) = -1.5708
    c: Tangent(g6,g5) = -1.5708
    c: Tangent(g5,g7) = -1.5708
    c: Tangent(g7,g4) = -1.5708
    c: Equal(g4,g5)
    c: Symmetric(g1,g0,g-2)
    c: Symmetric(g4,g5,g-2)
    c: Equal(g7,g2)
    c: Equal(g1,g5)
    c: DistanceX(g7,g7) = 3.9
    c: Radius(g5) = 1.95
    c: DistanceY(g1) = 4.725
    c: DistanceY(g4) = 31.275
FEATURE [PartDesign::Pad] Pad001
  BaseFeature = -> Pocket001
  Direction = (0,-1,-2e-16)
  Length = 1
  Length2 = 10
  Placement = pos=(0,0,0) rot=(0.57735,0.57735,0.57735;2.0944rad)
  Profile = -> Sketch003
  ReferenceAxis = -> Sketch003 [N_Axis]
  Reversed = true
  Type = 0
FEATURE [PartDesign::Plane] DatumPlane
  AttachmentOffset = pos=(0,0,0) rot=(1,0,0;0.785398rad)
  Length = 63.0271
  MapMode = 5
  Placement = pos=(0,0,0) rot=(1,0,0;2.35619rad)
  ResizeMode = 0
  Support = -> [XZ_Plane]
  Width = 97.8799
FEATURE [PartDesign::Mirrored] Mirrored
  BaseFeature = -> Pad001
  MirrorPlane = -> DatumPlane
  Originals = -> [Pocket001,Pad001]
  Placement = pos=(0,0,0) rot=(0.57735,0.57735,0.57735;2.0944rad)
FEATURE [PartDesign::Body] Body  label="Corner bracket 35x35"
  Group = -> [Sketch,Pad,Sketch001,Pocket,Sketch002,Pocket001,Sketch003,Pad001,DatumPlane,Mirrored]
  Origin = -> Origin
  Tip = -> Mirrored
  expr: Label = <<Corner bracket %s>> % Spreadsheet.A_dim + <<x%s>> % Spreadsheet.A_dim
PROVENANCE & LICENSES
A FreeCAD (.FCStd) document from a public repository crawl; recipes are the document's own serialized feature recipes (and, for linked parts, companion documents' recipes).
License: as declared in the source repository (recorded in the dataset sidecar).
